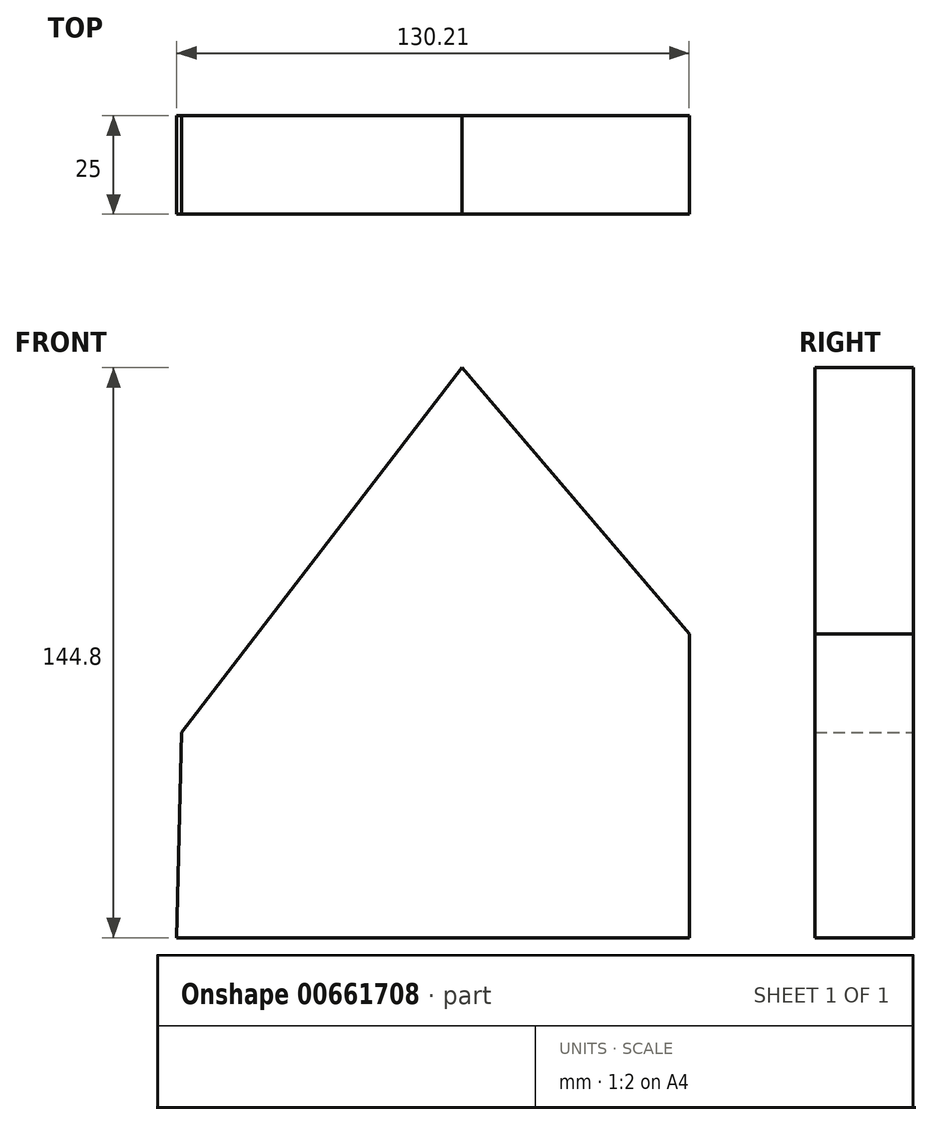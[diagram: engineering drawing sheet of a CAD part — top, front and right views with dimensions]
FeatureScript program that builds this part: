
annotation { "Feature Type Name" : "Feature", "Feature Type Description" : "" }
export const myFeature = defineFeature(function(context is Context, id is Id, definition is map)
    precondition{}
    {
        {
            var Q0;
            Q0=qCreatedBy(makeId("Front.planeOp"),FACE);
            var sketch = newSketch(context, id + "F0", { "sketchPlane" : qUnion([Q0])});
            skLineSegment(sketch, "E0", {"start": v(-64.9, -20.58) * mm, "end": v(6.35, 72.06) * mm});
            skLineSegment(sketch, "E1", {"start": v(6.35, 72.06) * mm, "end": v(64.08, 4.37) * mm});
            skLineSegment(sketch, "E2", {"start": v(64.08, 4.37) * mm, "end": v(64.08, -72.74) * mm});
            skLineSegment(sketch, "E3", {"start": v(64.08, -72.74) * mm, "end": v(-66.13, -72.74) * mm});
            skLineSegment(sketch, "E4", {"start": v(-66.13, -72.74) * mm, "end": v(-64.9, -20.58) * mm});
            skSolve(sketch);
        }
        {
            var Q0;
            Q0=makeQuery(id+"F0.imprint","IMPRINT",FACE,{"disambiguationData":[TD([[makeQuery(id+"F0.imprint","IMPRINT",EDGE,{"derivedFrom":sQuery(id+"F0.wireOp",EDGE,"E0")}),-1.0]])]});
            extrude(context, id + "F1", {"entities" : qUnion([Q0]), "depth" : 25 * mm, "offsetDistance" : 25 * mm});
        }
    });
